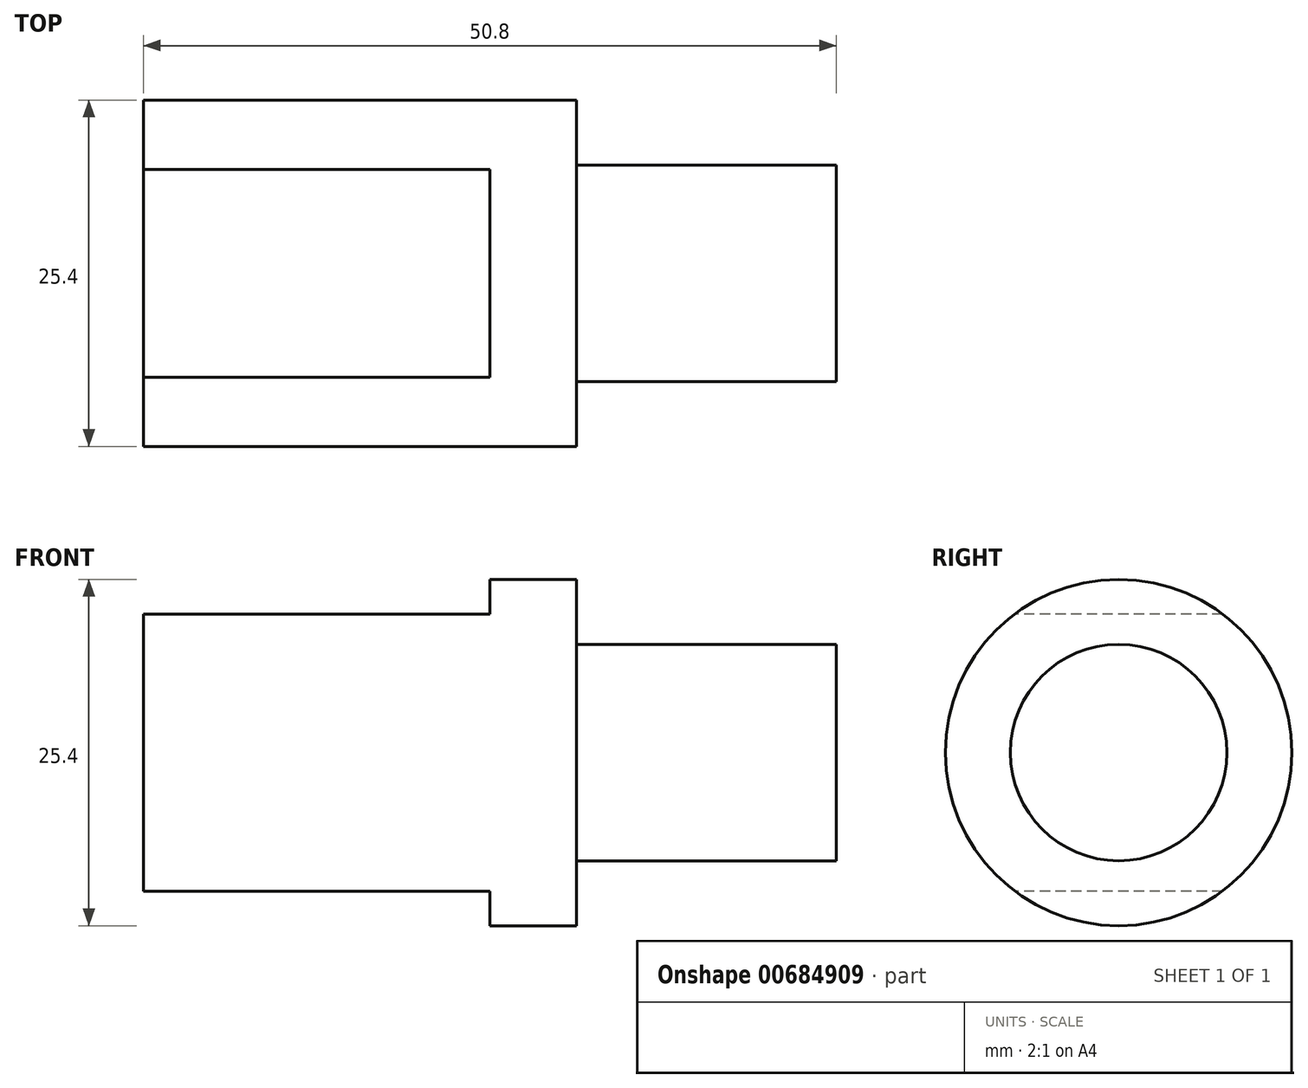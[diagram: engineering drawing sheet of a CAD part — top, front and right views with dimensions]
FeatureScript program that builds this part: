
annotation { "Feature Type Name" : "Feature", "Feature Type Description" : "" }
export const myFeature = defineFeature(function(context is Context, id is Id, definition is map)
    precondition{}
    {
        {
            var Q0;
            Q0=qCreatedBy(makeId("Front.planeOp"),FACE);
            var sketch = newSketch(context, id + "F0", { "sketchPlane" : qUnion([Q0])});
            skLineSegment(sketch, "E0", {"start": v(0, 12.7) * mm, "end": v(31.75, 12.7) * mm});
            skLineSegment(sketch, "E1", {"start": v(31.75, 12.7) * mm, "end": v(31.75, 7.94) * mm});
            skLineSegment(sketch, "E2", {"start": v(31.75, 7.94) * mm, "end": v(50.8, 7.94) * mm});
            skLineSegment(sketch, "E3", {"start": v(50.8, 7.94) * mm, "end": v(50.8, 0) * mm});
            skLineSegment(sketch, "E4", {"start": v(50.8, 0) * mm, "end": v(0, 0) * mm});
            skLineSegment(sketch, "E5", {"start": v(0, 0) * mm, "end": v(0, 12.7) * mm});
            skLineSegment(sketch, "E6", {"start": v(-24.53, 0) * mm, "end": v(74.02, 0) * mm, "construction": true});
            skSolve(sketch);
        }
        {
            var Q0;
            Q0 = qSketchRegion(id + "F0", true);
            var Q1;
            Q1=sQuery(id+"F0.wireOp",EDGE,"E6");
            revolve(context, id + "F1", {"surfaceOperationType" : NewSurfaceOperationType.NEW, "entities" : qUnion([Q0]), "axis" : qUnion([Q1]), "revolveType" : RevolveType.FULL});
        }
        {
            var Q0;
            Q0=makeQuery(id+"F1.opRevolve","SWEPT_FACE",FACE,{"disambiguationData":[OSD([sQuery(id+"F0.wireOp",EDGE,"E5")])]});
            var sketch = newSketch(context, id + "F2", { "sketchPlane" : qUnion([Q0])});
            skLineSegment(sketch, "E7", {"start": v(-7.62, 10.16) * mm, "end": v(7.62, 10.16) * mm});
            skLineSegment(sketch, "E8", {"start": v(-20.41, 0) * mm, "end": v(21.4, 0) * mm, "construction": true});
            skArc(sketch, "E9", {"start": v(7.62, 10.16) * mm, "mid": v(0, 12.7) * mm, "end": v(-7.62, 10.16) * mm});
            skLineSegment(sketch, "E10.MirrorCS", {"start": v(-7.62, -10.16) * mm, "end": v(7.62, -10.16) * mm});
            skArc(sketch, "E11.MirrorCS", {"start": v(7.62, -10.16) * mm, "mid": v(0, -12.7) * mm, "end": v(-7.62, -10.16) * mm});
            skSolve(sketch);
        }
        {
            var Q0;
            Q0 = qSketchRegion(id + "F2", true);
            extrude(context, id + "F3", {"entities" : qUnion([Q0]), "operationType" : NewBodyOperationType.REMOVE, "oppositeDirection" : true, "depth" : 25.4 * mm, "offsetDistance" : 25.4 * mm});
        }
    });
